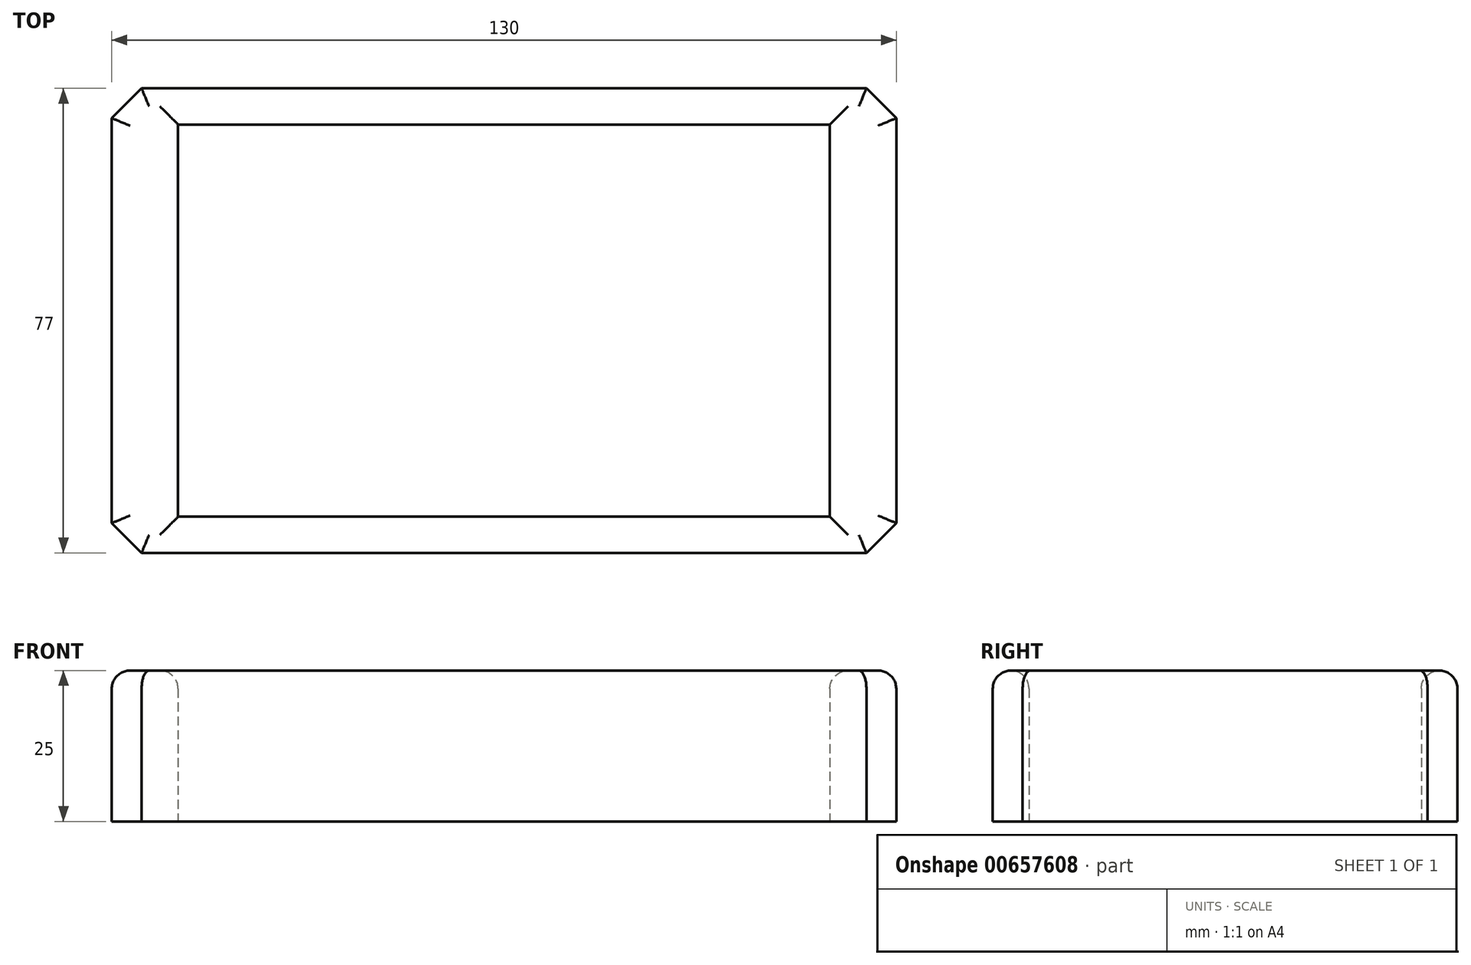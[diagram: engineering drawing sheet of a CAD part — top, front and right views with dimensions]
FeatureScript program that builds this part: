
annotation { "Feature Type Name" : "Feature", "Feature Type Description" : "" }
export const myFeature = defineFeature(function(context is Context, id is Id, definition is map)
    precondition{}
    {
        {
            var Q0;
            Q0=qCreatedBy(makeId("Top.planeOp"),FACE);
            var sketch = newSketch(context, id + "F0", { "sketchPlane" : qUnion([Q0])});
            skLineSegment(sketch, "E0.bottom", {"start": v(-60.06, 38.5) * mm, "end": v(60.06, 38.5) * mm});
            skLineSegment(sketch, "E0.top", {"start": v(-60.06, -38.5) * mm, "end": v(60.06, -38.5) * mm});
            skLineSegment(sketch, "E0.left", {"start": v(-65, 33.56) * mm, "end": v(-65, -33.56) * mm});
            skLineSegment(sketch, "E0.right", {"start": v(65, 33.56) * mm, "end": v(65, -33.56) * mm});
            skPoint(sketch, "E0.middle", {"position": v(0, 0) * mm});
            skLineSegment(sketch, "E1", {"start": v(-60.06, 38.5) * mm, "end": v(-65, 33.56) * mm});
            skLineSegment(sketch, "E2.MirrorCS", {"start": v(-60.06, -38.5) * mm, "end": v(-65, -33.56) * mm});
            skLineSegment(sketch, "E3.MirrorCS", {"start": v(60.06, 38.5) * mm, "end": v(65, 33.56) * mm});
            skLineSegment(sketch, "E4.MirrorCS", {"start": v(60.06, -38.5) * mm, "end": v(65, -33.56) * mm});
            skPoint(sketch, "E5.orphan", {"position": v(-65, 38.5) * mm});
            skPoint(sketch, "E6.orphan", {"position": v(-65, -38.5) * mm});
            skPoint(sketch, "E7.orphan", {"position": v(65, -38.5) * mm});
            skPoint(sketch, "E8.orphan", {"position": v(65, 38.5) * mm});
            skLineSegment(sketch, "E9.bottom", {"start": v(-54, 32.5) * mm, "end": v(54, 32.5) * mm});
            skLineSegment(sketch, "E9.top", {"start": v(-54, -32.5) * mm, "end": v(54, -32.5) * mm});
            skLineSegment(sketch, "E9.left", {"start": v(-54, 32.5) * mm, "end": v(-54, -32.5) * mm});
            skLineSegment(sketch, "E9.right", {"start": v(54, 32.5) * mm, "end": v(54, -32.5) * mm});
            skSolve(sketch);
        }
        {
            var Q0;
            Q0=makeQuery(id+"F0.imprint","IMPRINT",FACE,{"disambiguationData":[TD([[makeQuery(id+"F0.imprint","IMPRINT",EDGE,{"derivedFrom":sQuery(id+"F0.wireOp",EDGE,"E0.bottom")}),-1.0]])]});
            extrude(context, id + "F1", {"entities" : qUnion([Q0]), "depth" : 25 * mm, "offsetDistance" : 25 * mm});
        }
        {
            var Q0;
            Q0=makeQuery(id+"F1.opExtrude","CAP_FACE",FACE,{"disambiguationData":[OSD([sQuery(id+"F0.wireOp",EDGE,"E0.bottom"),sQuery(id+"F0.wireOp",EDGE,"E0.top"),sQuery(id+"F0.wireOp",EDGE,"E0.left"),sQuery(id+"F0.wireOp",EDGE,"E0.right"),sQuery(id+"F0.wireOp",EDGE,"E1"),sQuery(id+"F0.wireOp",EDGE,"E2.MirrorCS"),sQuery(id+"F0.wireOp",EDGE,"E3.MirrorCS"),sQuery(id+"F0.wireOp",EDGE,"E4.MirrorCS"),sQuery(id+"F0.wireOp",EDGE,"E9.bottom"),sQuery(id+"F0.wireOp",EDGE,"E9.top"),sQuery(id+"F0.wireOp",EDGE,"E9.left"),sQuery(id+"F0.wireOp",EDGE,"E9.right")])],"isStart":false});
            fillet(context, id + "F2", {"entities" : qUnion([Q0]), "radius" : 3 * mm, "tangentPropagation" : true, "allowEdgeOverflow" : false});
        }
    });
